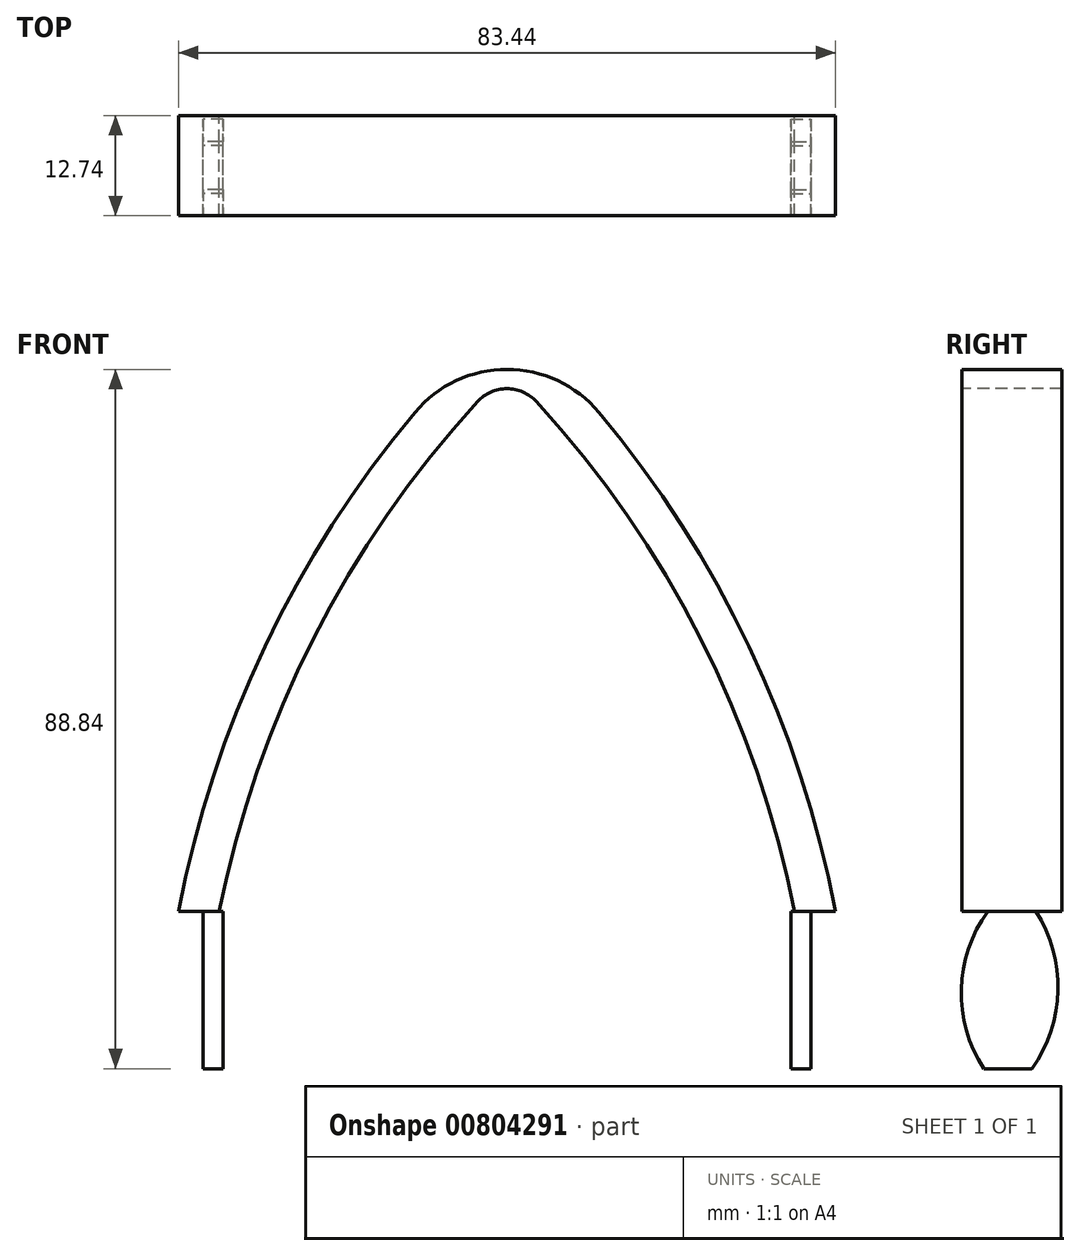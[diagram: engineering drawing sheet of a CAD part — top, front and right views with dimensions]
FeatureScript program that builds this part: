
annotation { "Feature Type Name" : "Feature", "Feature Type Description" : "" }
export const myFeature = defineFeature(function(context is Context, id is Id, definition is map)
    precondition{}
    {
        {
            var Q0;
            Q0=qCreatedBy(makeId("Front.planeOp"),FACE);
            var sketch = newSketch(context, id + "F0", { "sketchPlane" : qUnion([Q0])});
            skArc(sketch, "E0", {"start": v(0, 76.57) * mm, "mid": v(-26.88, 42.01) * mm, "end": v(-41.72, 0.83) * mm});
            skArc(sketch, "E1", {"start": v(41.72, 0.83) * mm, "mid": v(26.88, 42.01) * mm, "end": v(0, 76.57) * mm});
            skArc(sketch, "E2.0", {"start": v(0, 69.5) * mm, "mid": v(-23.35, 37.86) * mm, "end": v(-36.54, 0.83) * mm});
            skArc(sketch, "E2.1", {"start": v(36.54, 0.83) * mm, "mid": v(23.35, 37.86) * mm, "end": v(0, 69.5) * mm});
            skLineSegment(sketch, "E3", {"start": v(-41.72, 0.83) * mm, "end": v(-36.54, 0.83) * mm});
            skLineSegment(sketch, "E4", {"start": v(36.54, 0.83) * mm, "end": v(41.72, 0.83) * mm});
            skSolve(sketch);
        }
        {
            var Q0;
            Q0=makeQuery(id+"F0.imprint","IMPRINT",FACE,{"disambiguationData":[TD([[makeQuery(id+"F0.imprint","IMPRINT",EDGE,{"derivedFrom":sQuery(id+"F0.wireOp",EDGE,"E0")}),1.0]])]});
            extrude(context, id + "F1", {"entities" : qUnion([Q0]), "depth" : 12.7 * mm, "offsetDistance" : 25.4 * mm});
        }
        {
            var Q0;
            Q0=makeQuery(id+"F1.opExtrude","SWEPT_EDGE",EDGE,{"disambiguationData":[OSD([sQuery(id+"F0.wireOp",EDGE,"E0"),sQuery(id+"F0.wireOp",EDGE,"E1")])]});
            fillet(context, id + "F2", {"entities" : qUnion([Q0]), "radius" : 15.24 * mm, "tangentPropagation" : true, "allowEdgeOverflow" : false});
        }
        {
            var Q0;
            Q0=makeQuery(id+"F1.opExtrude","SWEPT_EDGE",EDGE,{"disambiguationData":[OSD([sQuery(id+"F0.wireOp",EDGE,"E2.0"),sQuery(id+"F0.wireOp",EDGE,"E2.1")])]});
            fillet(context, id + "F3", {"entities" : qUnion([Q0]), "radius" : 5.08 * mm, "tangentPropagation" : true, "allowEdgeOverflow" : false});
        }
        {
            var Q0;
            Q0=qCreatedBy(makeId("Right.planeOp"),FACE);
            cPlane(context, id + "F4", {"entities" : qUnion([Q0]), "cplaneType" : CPlaneType.OFFSET, "offset" : 37.34 * mm, "width" : 152.4 * mm, "height" : 152.4 * mm});
        }
        {
            var Q0;
            Q0=qCreatedBy(id+"F4.planeOp",FACE);
            var sketch = newSketch(context, id + "F5", { "sketchPlane" : qUnion([Q0])});
            skArc(sketch, "E5", {"start": v(-9.4, 0.83) * mm, "mid": v(-12.73, -9.1) * mm, "end": v(-9.9, -19.16) * mm});
            skArc(sketch, "E6", {"start": v(-3.8, -19.16) * mm, "mid": v(-0.46, -9.24) * mm, "end": v(-3.3, 0.83) * mm});
            skLineSegment(sketch, "E7", {"start": v(-3.3, 0.83) * mm, "end": v(-9.4, 0.83) * mm});
            skLineSegment(sketch, "E8", {"start": v(-9.9, -19.16) * mm, "end": v(-3.8, -19.16) * mm});
            skSolve(sketch);
        }
        {
            var Q0;
            Q0=makeQuery(id+"F5.imprint","IMPRINT",FACE,{"disambiguationData":[TD([[makeQuery(id+"F5.imprint","IMPRINT",EDGE,{"derivedFrom":sQuery(id+"F5.wireOp",EDGE,"E5")}),1.0]])]});
            extrude(context, id + "F6", {"entities" : qUnion([Q0]), "operationType" : NewBodyOperationType.ADD, "endBound" : BoundingType.SYMMETRIC, "oppositeDirection" : true, "depth" : 2.54 * mm, "offsetDistance" : 25.4 * mm});
        }
        {
            var Q0;
            Q0=qCreatedBy(makeId("Right.planeOp"),FACE);
            cPlane(context, id + "F7", {"entities" : qUnion([Q0]), "cplaneType" : CPlaneType.OFFSET, "offset" : 37.34 * mm, "oppositeDirection" : true, "width" : 152.4 * mm, "height" : 152.4 * mm});
        }
        {
            var Q0;
            Q0=qCreatedBy(id+"F7.planeOp",FACE);
            var sketch = newSketch(context, id + "F8", { "sketchPlane" : qUnion([Q0])});
            skArc(sketch, "E9", {"start": v(-9.4, 0.83) * mm, "mid": v(-12.73, -9.1) * mm, "end": v(-9.9, -19.16) * mm});
            skArc(sketch, "E10", {"start": v(-3.8, -19.16) * mm, "mid": v(-0.46, -9.24) * mm, "end": v(-3.3, 0.83) * mm});
            skLineSegment(sketch, "E11", {"start": v(-9.9, -19.16) * mm, "end": v(-3.8, -19.16) * mm});
            skLineSegment(sketch, "E12", {"start": v(-9.4, 0.83) * mm, "end": v(-3.3, 0.83) * mm});
            skPoint(sketch, "E13", {"position": v(-6.35, 0.83) * mm});
            skSolve(sketch);
        }
        {
            var Q0;
            Q0=makeQuery(id+"F8.imprint","IMPRINT",FACE,{"disambiguationData":[TD([[makeQuery(id+"F8.imprint","IMPRINT",EDGE,{"derivedFrom":sQuery(id+"F8.wireOp",EDGE,"E9")}),1.0]])]});
            extrude(context, id + "F9", {"entities" : qUnion([Q0]), "operationType" : NewBodyOperationType.ADD, "endBound" : BoundingType.SYMMETRIC, "depth" : 2.54 * mm, "offsetDistance" : 25.4 * mm});
        }
    });
